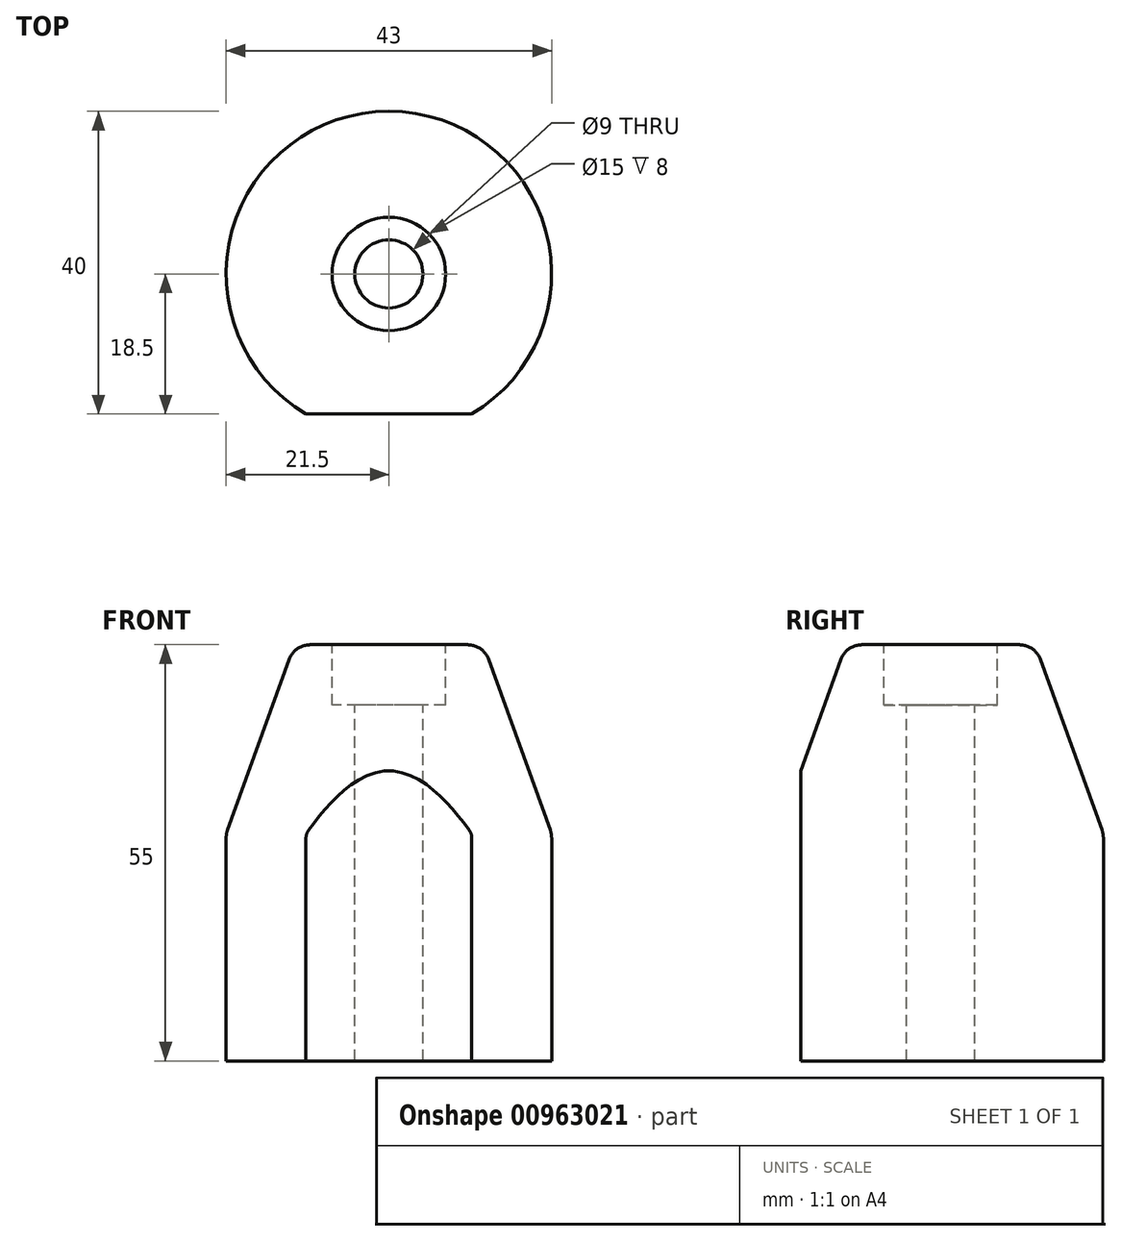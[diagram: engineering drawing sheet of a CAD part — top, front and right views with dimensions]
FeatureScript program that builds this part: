
annotation { "Feature Type Name" : "Feature", "Feature Type Description" : "" }
export const myFeature = defineFeature(function(context is Context, id is Id, definition is map)
    precondition{}
    {
        {
            var Q0;
            Q0=qCreatedBy(makeId("Top.planeOp"),FACE);
            var sketch = newSketch(context, id + "F0", { "sketchPlane" : qUnion([Q0])});
            skCircle(sketch, "E0", {"center": v(0, 0) * mm, "radius": 21.5 * mm});
            skSolve(sketch);
        }
        {
            var Q0;
            Q0 = qSketchRegion(id + "F0", true);
            extrude(context, id + "F1", {"entities" : qUnion([Q0]), "depth" : 30 * mm, "offsetDistance" : 25 * mm});
        }
        {
            var Q0;
            Q0=qCreatedBy(makeId("Top.planeOp"),FACE);
            cPlane(context, id + "F2", {"entities" : qUnion([Q0]), "cplaneType" : CPlaneType.OFFSET, "offset" : 55 * mm, "width" : 150 * mm, "height" : 150 * mm});
        }
        {
            var Q0;
            Q0=qCreatedBy(id+"F2.planeOp",FACE);
            var sketch = newSketch(context, id + "F3", { "sketchPlane" : qUnion([Q0])});
            skCircle(sketch, "E1", {"center": v(0, 0) * mm, "radius": 12.5 * mm});
            skSolve(sketch);
        }
        {
            var Q1;
            Q1=makeQuery(id+"F3.imprint","IMPRINT",FACE,{"disambiguationData":[TD([[makeQuery(id+"F3.imprint","IMPRINT",EDGE,{"derivedFrom":sQuery(id+"F3.wireOp",EDGE,"E1")}),1.0]])]});
            var Q2;
            Q2=makeQuery(id+"F1.opExtrude","CAP_FACE",FACE,{"disambiguationData":[OSD([sQuery(id+"F0.wireOp",EDGE,"E0")])],"isStart":false});
            loft(context, id + "F4", {"operationType" : NewBodyOperationType.ADD, "sheetProfilesArray" : [{ "sheetProfileEntities" : qUnion([Q1]) }, { "sheetProfileEntities" : qUnion([Q2]) }]});
        }
        {
            var Q0;
            Q0=makeQuery(id+"F4.opLoft","CAP_FACE",FACE,{"disambiguationData":[OSD([makeQuery(id+"F3.imprint","IMPRINT",FACE,{"disambiguationData":[TD([[makeQuery(id+"F3.imprint","IMPRINT",EDGE,{"derivedFrom":sQuery(id+"F3.wireOp",EDGE,"E1")}),1.0]])]})])],"isStart":true});
            var sketch = newSketch(context, id + "F5", { "sketchPlane" : qUnion([Q0])});
            skPoint(sketch, "E2", {"position": v(0, 0) * mm});
            skSolve(sketch);
        }
        {
            var Q0;
            Q0=sQuery(id+"F5.wireOp",VERTEX,"E2");
            var Q1;
            Q1=makeQuery(id+"F1.opExtrude","SWEPT_BODY",BODY,{"disambiguationData":[OSD([sQuery(id+"F0.wireOp",EDGE,"E0")])]});
            hole(context, id + "F6", {"style" : HoleStyle.C_BORE, "endStyle" : HoleEndStyle.THROUGH, "holeDiameter" : 9 * mm, "cBoreDiameter" : 15 * mm, "cBoreDepth" : 8 * mm, "majorDiameter" : 5 * mm, "isTappedThrough" : true, "tappedDepth" : 12.6 * mm, "tapClearance" : 3, "startFromSketch" : true, "locations" : qUnion([Q0]), "scope" : qUnion([Q1])});
        }
        {
            var Q0;
            Q0=qCreatedBy(makeId("Front.planeOp"),FACE);
            cPlane(context, id + "F7", {"entities" : qUnion([Q0]), "cplaneType" : CPlaneType.OFFSET, "offset" : 21.5 * mm, "width" : 150 * mm, "height" : 150 * mm});
        }
        {
            var Q0;
            Q0=qCreatedBy(id+"F7.planeOp",FACE);
            var sketch = newSketch(context, id + "F8", { "sketchPlane" : qUnion([Q0])});
            skPoint(sketch, "E3", {"position": v(40.03, 0) * mm});
            skPoint(sketch, "E4", {"position": v(-45, 0) * mm});
            skPoint(sketch, "E5", {"position": v(-45, 45) * mm});
            skPoint(sketch, "E6", {"position": v(40.03, 45) * mm});
            skLineSegment(sketch, "E7.bottom", {"start": v(40.03, 0) * mm, "end": v(-45, 0) * mm});
            skLineSegment(sketch, "E7.top", {"start": v(40.03, 45) * mm, "end": v(-45, 45) * mm});
            skLineSegment(sketch, "E7.left", {"start": v(40.03, 0) * mm, "end": v(40.03, 45) * mm});
            skLineSegment(sketch, "E7.right", {"start": v(-45, 0) * mm, "end": v(-45, 45) * mm});
            skSolve(sketch);
        }
        {
            var Q0;
            Q0=makeQuery(id+"F8.imprint","IMPRINT",FACE,{"disambiguationData":[TD([[makeQuery(id+"F8.imprint","IMPRINT",EDGE,{"derivedFrom":sQuery(id+"F8.wireOp",EDGE,"E7.bottom")}),-1.0]])]});
            extrude(context, id + "F9", {"entities" : qUnion([Q0]), "operationType" : NewBodyOperationType.REMOVE, "oppositeDirection" : true, "depth" : 3 * mm, "offsetDistance" : 25 * mm});
        }
        {
            var Q0;
            Q0=makeQuery(id+"F4.opLoft","MID_CAP_EDGE",EDGE,{"disambiguationData":[OSD([sQuery(id+"F3.wireOp",EDGE,"E1")])],"capPos":0.0});
            fillet(context, id + "F10", {"entities" : qUnion([Q0]), "radius" : 3 * mm, "tangentPropagation" : true, "allowEdgeOverflow" : false});
        }
        {
            var Q0;
            {var subQ0=sQuery(id+"F0.wireOp",EDGE,"E0");Q0=makeQuery(id+"F4.boolean.opBoolean","MERGE",EDGE,{"derivedFrom":[makeQuery(id+"F1.opExtrude","CAP_EDGE",EDGE,{"disambiguationData":[OSD([subQ0])],"isStart":false}),makeQuery(id+"F4.opLoft","MID_CAP_EDGE",EDGE,{"disambiguationData":[OSD([subQ0])],"capPos":1.0})]});}
            fillet(context, id + "F11", {"entities" : qUnion([Q0]), "radius" : 3 * mm, "tangentPropagation" : true, "allowEdgeOverflow" : false});
        }
    });
